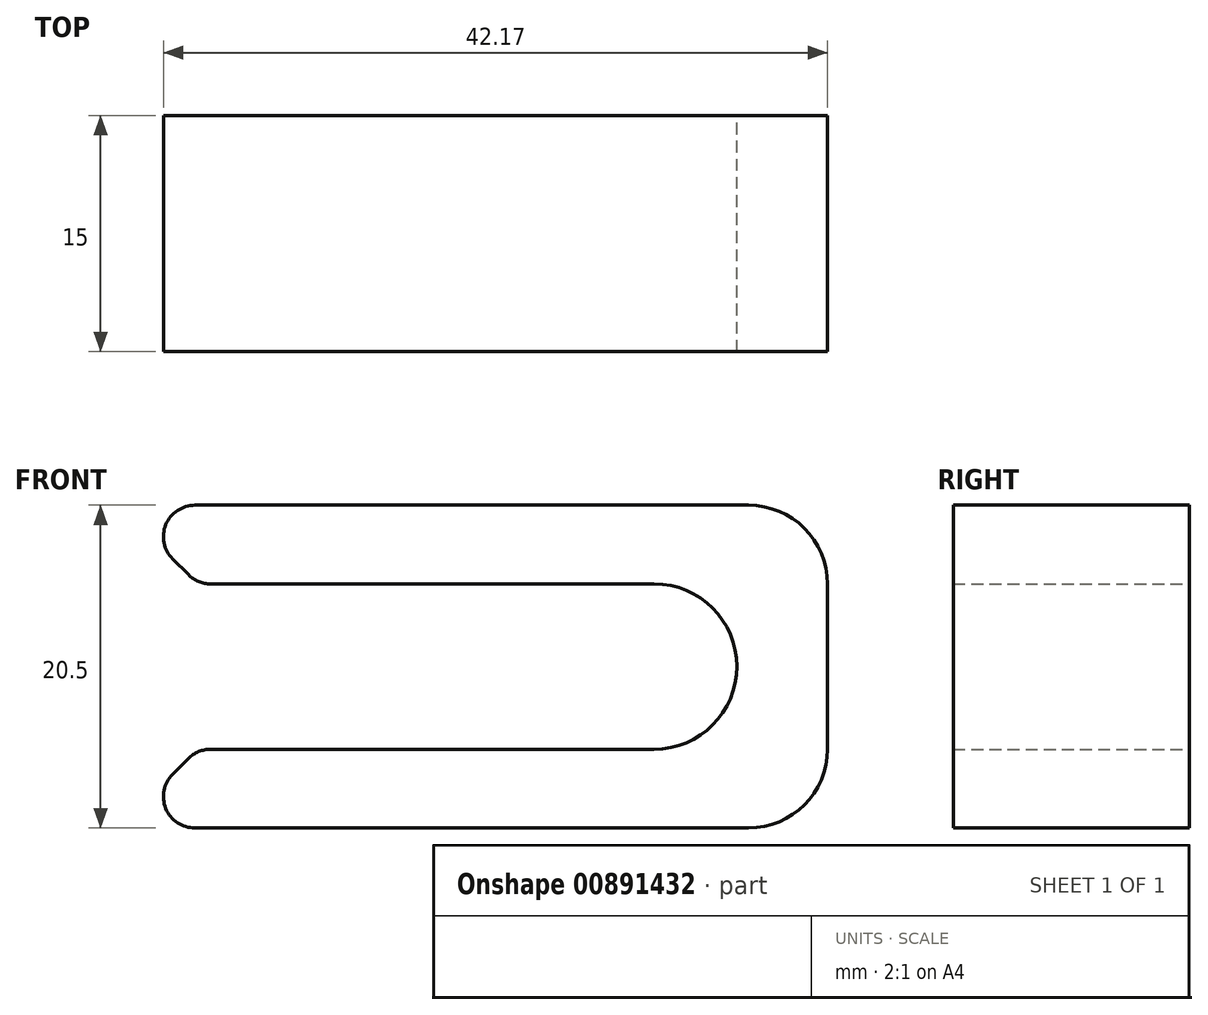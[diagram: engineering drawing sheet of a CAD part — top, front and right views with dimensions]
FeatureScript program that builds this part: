
annotation { "Feature Type Name" : "Feature", "Feature Type Description" : "" }
export const myFeature = defineFeature(function(context is Context, id is Id, definition is map)
    precondition{}
    {
        {
            var Q0;
            Q0=qCreatedBy(makeId("Front.planeOp"),FACE);
            var sketch = newSketch(context, id + "F0", { "sketchPlane" : qUnion([Q0])});
            skLineSegment(sketch, "E0", {"start": v(-25, 0) * mm, "end": v(20, 0) * mm});
            skLineSegment(sketch, "E1", {"start": v(20, 0) * mm, "end": v(20, 20.5) * mm});
            skLineSegment(sketch, "E2", {"start": v(20, 20.5) * mm, "end": v(-25, 20.5) * mm});
            skLineSegment(sketch, "E3", {"start": v(-25, 20.5) * mm, "end": v(-20, 15.5) * mm});
            skLineSegment(sketch, "E4", {"start": v(-20, 15.5) * mm, "end": v(9, 15.5) * mm});
            skLineSegment(sketch, "E5", {"start": v(-25, 0) * mm, "end": v(-20, 5) * mm});
            skLineSegment(sketch, "E6", {"start": v(-20, 5) * mm, "end": v(9, 5) * mm});
            skArc(sketch, "E7", {"start": v(9, 5) * mm, "mid": v(14.25, 10.25) * mm, "end": v(9, 15.5) * mm});
            skSolve(sketch);
        }
        {
            var Q0;
            Q0 = qSketchRegion(id + "F0", true);
            extrude(context, id + "F1", {"entities" : qUnion([Q0]), "depth" : 15 * mm, "offsetDistance" : 25 * mm});
        }
        {
            var Q0;
            Q0=makeQuery(id+"F1.opExtrude","SWEPT_EDGE",EDGE,{"disambiguationData":[OSD([sQuery(id+"F0.wireOp",EDGE,"E1"),sQuery(id+"F0.wireOp",EDGE,"E2")])]});
            var Q1;
            Q1=makeQuery(id+"F1.opExtrude","SWEPT_EDGE",EDGE,{"disambiguationData":[OSD([sQuery(id+"F0.wireOp",EDGE,"E0"),sQuery(id+"F0.wireOp",EDGE,"E1")])]});
            fillet(context, id + "F2", {"entities" : qUnion([Q0, Q1]), "radius" : 5 * mm, "tangentPropagation" : true, "allowEdgeOverflow" : false});
        }
        {
            var Q0;
            Q0=makeQuery(id+"F1.opExtrude","SWEPT_EDGE",EDGE,{"disambiguationData":[OSD([sQuery(id+"F0.wireOp",EDGE,"E2"),sQuery(id+"F0.wireOp",EDGE,"E3")])]});
            var Q1;
            Q1=makeQuery(id+"F1.opExtrude","SWEPT_EDGE",EDGE,{"disambiguationData":[OSD([sQuery(id+"F0.wireOp",EDGE,"E5"),sQuery(id+"F0.wireOp",EDGE,"E6")])]});
            var Q2;
            Q2=makeQuery(id+"F1.opExtrude","SWEPT_EDGE",EDGE,{"disambiguationData":[OSD([sQuery(id+"F0.wireOp",EDGE,"E0"),sQuery(id+"F0.wireOp",EDGE,"E5")])]});
            var Q3;
            Q3=makeQuery(id+"F1.opExtrude","SWEPT_EDGE",EDGE,{"disambiguationData":[OSD([sQuery(id+"F0.wireOp",EDGE,"E3"),sQuery(id+"F0.wireOp",EDGE,"E4")])]});
            fillet(context, id + "F3", {"entities" : qUnion([Q0, Q1, Q2, Q3]), "radius" : 2 * mm, "tangentPropagation" : true, "allowEdgeOverflow" : false});
        }
    });
